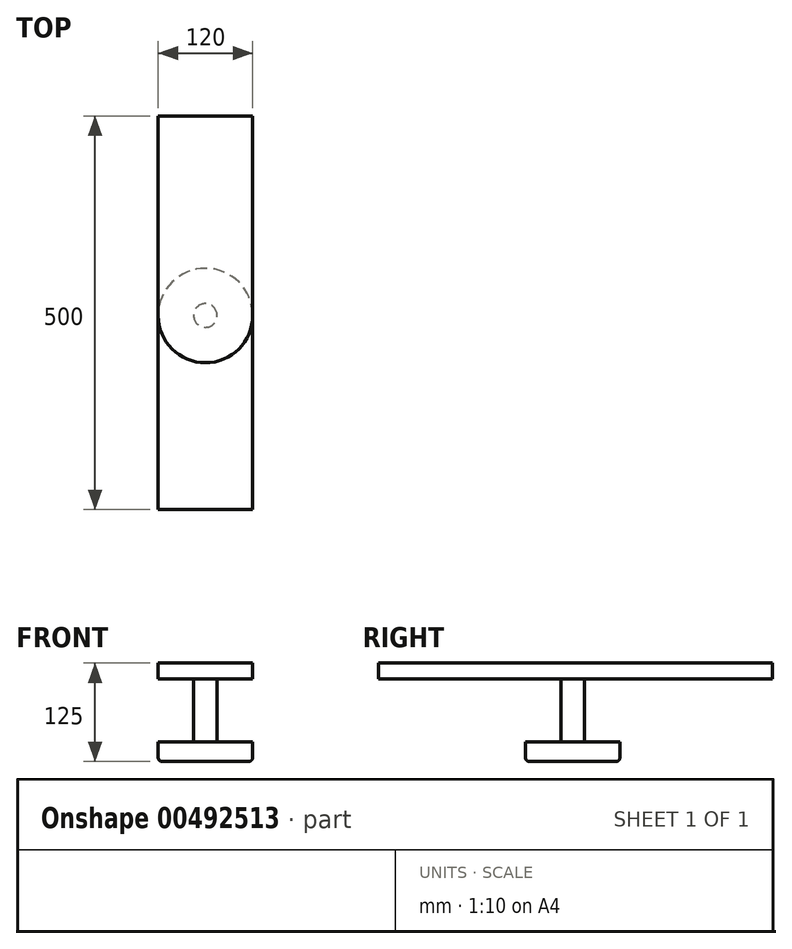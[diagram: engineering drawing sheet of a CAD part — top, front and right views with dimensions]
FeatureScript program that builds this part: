
annotation { "Feature Type Name" : "Feature", "Feature Type Description" : "" }
export const myFeature = defineFeature(function(context is Context, id is Id, definition is map)
    precondition{}
    {
        {
            var Q0;
            Q0=qCreatedBy(makeId("Top.planeOp"),FACE);
            var sketch = newSketch(context, id + "F0", { "sketchPlane" : qUnion([Q0])});
            skLineSegment(sketch, "E0.bottom", {"start": v(-60, -250) * mm, "end": v(60, -250) * mm});
            skLineSegment(sketch, "E0.top", {"start": v(-60, 250) * mm, "end": v(60, 250) * mm});
            skLineSegment(sketch, "E0.left", {"start": v(-60, -250) * mm, "end": v(-60, 250) * mm});
            skLineSegment(sketch, "E0.right", {"start": v(60, -250) * mm, "end": v(60, 250) * mm});
            skPoint(sketch, "E0.middle", {"position": v(0, 0) * mm});
            skSolve(sketch);
        }
        {
            var Q0;
            Q0 = qSketchRegion(id + "F0", true);
            extrude(context, id + "F1", {"entities" : qUnion([Q0]), "depth" : 20 * mm});
        }
        {
            var Q0;
            Q0=makeQuery(id+"F1.opExtrude","CAP_FACE",FACE,{"disambiguationData":[OSD([sQuery(id+"F0.wireOp",EDGE,"E0.bottom"),sQuery(id+"F0.wireOp",EDGE,"E0.top"),sQuery(id+"F0.wireOp",EDGE,"E0.left"),sQuery(id+"F0.wireOp",EDGE,"E0.right")])],"isStart":false});
            var sketch = newSketch(context, id + "F2", { "sketchPlane" : qUnion([Q0])});
            skCircle(sketch, "E1", {"center": v(0, -3.44) * mm, "radius": 15 * mm});
            skSolve(sketch);
        }
        {
            var Q0;
            Q0 = qSketchRegion(id + "F2", true);
            extrude(context, id + "F3", {"entities" : qUnion([Q0]), "operationType" : NewBodyOperationType.ADD, "oppositeDirection" : true, "depth" : 100 * mm});
        }
        {
            var Q0;
            Q0=makeQuery(id+"F3.opExtrude","CAP_FACE",FACE,{"disambiguationData":[OSD([sQuery(id+"F2.wireOp",EDGE,"E1")])],"isStart":false});
            var sketch = newSketch(context, id + "F4", { "sketchPlane" : qUnion([Q0])});
            skCircle(sketch, "E2", {"center": v(0, 3.44) * mm, "radius": 60 * mm});
            skSolve(sketch);
        }
        {
            var Q0;
            Q0 = qSketchRegion(id + "F4", true);
            extrude(context, id + "F5", {"entities" : qUnion([Q0]), "operationType" : NewBodyOperationType.ADD, "depth" : 25 * mm, "offsetDistance" : 25 * mm});
        }
        {
            var Q0;
            Q0=makeQuery(id+"F5.opExtrude","CAP_EDGE",EDGE,{"disambiguationData":[OSD([sQuery(id+"F4.wireOp",EDGE,"E2")])],"isStart":false});
            fillet(context, id + "F6", {"entities" : qUnion([Q0]), "radius" : 5 * mm, "tangentPropagation" : true, "allowEdgeOverflow" : false});
        }
    });
